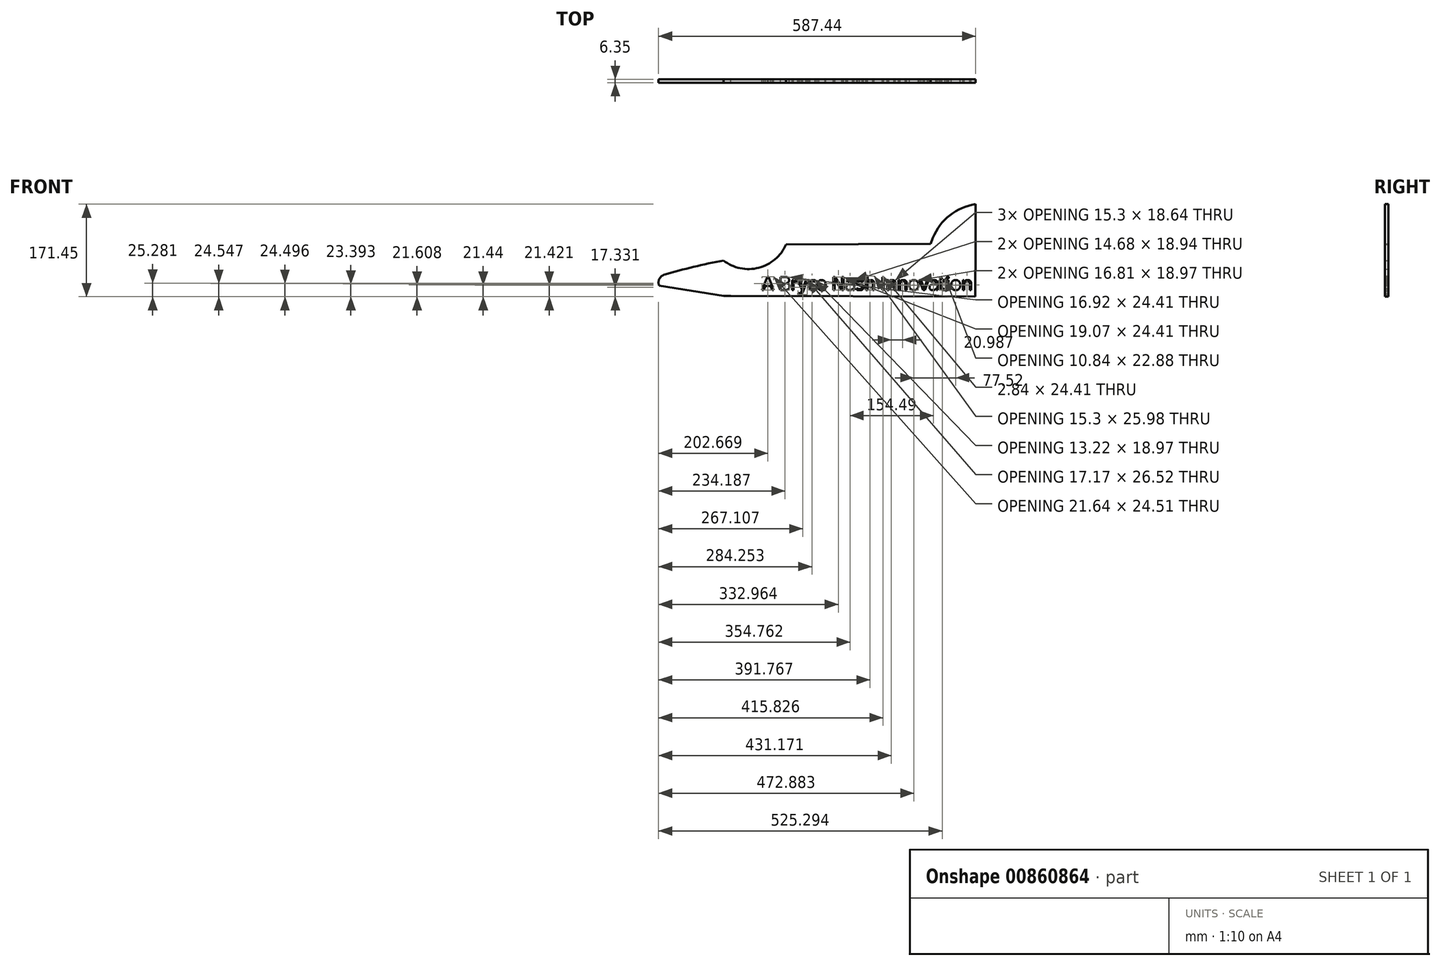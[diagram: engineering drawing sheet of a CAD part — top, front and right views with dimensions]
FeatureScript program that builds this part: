
annotation { "Feature Type Name" : "Feature", "Feature Type Description" : "" }
export const myFeature = defineFeature(function(context is Context, id is Id, definition is map)
    precondition{}
    {
        {
            var Q0;
            Q0=qCreatedBy(makeId("Front.planeOp"),FACE);
            var sketch = newSketch(context, id + "F0", { "sketchPlane" : qUnion([Q0])});
            skLineSegment(sketch, "E0.bottom", {"start": v(-87.58, 29.58) * mm, "end": v(180.02, 31.01) * mm});
            skLineSegment(sketch, "E0.right", {"start": v(263.6, 31.46) * mm, "end": v(262.71, -67.01) * mm});
            skArc(sketch, "E1", {"start": v(-203.65, 0) * mm, "mid": v(-258.8, -11.78) * mm, "end": v(-313.25, -26.43) * mm});
            skLineSegment(sketch, "E2.trimOffspring", {"start": v(-189.78, -65.7) * mm, "end": v(262.71, -67.01) * mm});
            skArc(sketch, "E3", {"start": v(-203.65, -65.66) * mm, "mid": v(-196.71, -65.73) * mm, "end": v(-189.78, -65.7) * mm});
            skPoint(sketch, "E4.orphan", {"position": v(-203.65, -65.66) * mm});
            skPoint(sketch, "E5.visualSharp", {"position": v(-326.9, -30.58) * mm});
            skArc(sketch, "E5.filletArc", {"start": v(-313.25, -26.43) * mm, "mid": v(-322.48, -34.4) * mm, "end": v(-322.6, -46.6) * mm});
            skArc(sketch, "E6", {"start": v(-203.65, 0) * mm, "mid": v(-138.43, -13.4) * mm, "end": v(-87.58, 29.58) * mm});
            skLineSegment(sketch, "E7.left", {"start": v(263.6, 31.46) * mm, "end": v(263.6, 104.44) * mm});
            skArc(sketch, "E8", {"start": v(263.6, 104.44) * mm, "mid": v(215.52, 83.77) * mm, "end": v(184.3, 41.8) * mm});
            skLineSegment(sketch, "E9", {"start": v(184.3, 41.8) * mm, "end": v(180.02, 31.01) * mm});
            skText(sketch, "E10", { "text": "A Bryce Nash Innovation", "fontName": "OpenSans-Regular.ttf"});
            skLineSegment(sketch, "E11", {"start": v(-203.65, -65.66) * mm, "end": v(-322.6, -46.6) * mm});
            const initialGuessF0  = {"E10": [-0.132, -0.05472, 1, 0, 0.02462]};
            skSetInitialGuess(sketch, initialGuessF0);
            skSolve(sketch);
        }
        {
            var Q0;
            Q0 = qSketchRegion(id + "F0", true);
            extrude(context, id + "F1", {"entities" : qUnion([Q0]), "depth" : 6.35 * mm, "offsetDistance" : 25.4 * mm});
        }
    });
